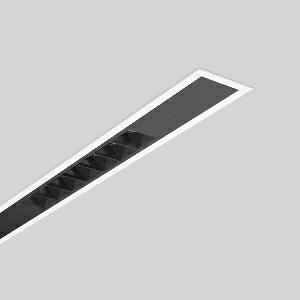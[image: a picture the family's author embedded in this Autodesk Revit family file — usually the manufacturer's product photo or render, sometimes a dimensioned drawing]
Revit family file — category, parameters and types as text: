
# Revit family: less_is_more_beamline_312465_002_76_12bc
name_source: partatom
category: Lighting Fixtures
units: mm (PartAtom-declared; Revit-internal decimal feet)

## family parameters
Cut with Voids When Loaded = No
Host = Face
Light Source = No
Part Type = Normal
Room Calculation Point = No
Round Connector Dimension = Use Diameter
Shared = No

## types (1)
- LESS IS MORE BEAMLINE (1 x LED Modul 930, 1025 lm, 3000)
    Apparent Load = 23 VA
    CIE Flux Codes = 100 100 100 100 100
    Color Rendering = 90
    Color Temperature = 3000
    Default Elevation = 1800 mm
    Description = Series: LESS IS MORE BEAMLINE
Linear recessed ceiling and wall luminaire for aesthetically sophisticated lighting. Luminaire with two LED light units. Housing: extruded aluminium profile, powder-coated. End cap aluminium powder-coated. LED light unit with MRS technology: Mini-Reflector-System made of metallised thermoplastic with prismatic black glare-suppressing frame for pleasant glare-free light (RUG < 10). Each LED light unit has 7 reflector elements. Narrow beam light distribution. Ceiling installation with pre-assembled SBS mounting system. LED unit with integrated converter interchangeable and removable. Suitable for through-wiring. 
Colour: traffic white, matt (RAL 9016)
Length: 1141 mm
Width: 71 mm
Height: 1.5 mm
Cut-out length: 1128 mm
Cut-out width: 60 mm
Recess height: 125 mm
Luminaire: recess height: 106 mm
Lamp: LED
Socket: without socket
Colour temperature: 3000K
Colour rendering index (CRI): 90
System power: 23 W
Rated luminous flux: 2050 lm
Luminous efficiency: 89 lm/W
Control gear: Converter, dimmable, DALI
Protection class: I
Type of protection: IP 20
    Height = 0 mm  [stored 0 ft]
    Lamp = 1 x LED Modul 930
    Lamp Light Flux = 1025 lm
    Lamp count = 1
    Length = 1141 mm
    Lifetime = 50000 h
    Luminous efficacy = 89 lm/W
    Manufacturer = RZB
    ModVariant = No
    Model = 312465.002.76
    Mounting Place = Ceiling, Wall
    Mounting Type = Recessed
    Number of Poles = 1
    OnlyDefault = Yes
    Power Factor = 1
    Product Name = LESS IS MORE BEAMLINE
    Product group = Recessed LED linear luminaires
    ProductGroupID = 407
    Protection Class = Protection class I
    Protection Degree = IP 20
    RLX_Detail_Level = 1
    RLX_Emergency_Light_Flux = 0 lm
    RLX_Emergency_Type = 0
    RLX_Emergency_Type_DB = No
    RlxData = <blob elided: 23713 chars, md5=9573ce2d>
    Socket = socket
    Standby Power = 0 W
    System Light Flux = 2050 lm
    System Power = 23 W
    Type Comments = Product without accessories
    Type Image = 312465.002.jpg
    URL = http://relux.com
    VarID = ---
    Voltage = 230 V
    Voltage Range = 220-240 V
    Weight = 0.00 kg
    Width = 71 mm

note: [stored X ft] marks values corroborated as IEEE doubles in the binary element streams (Revit-internal decimal feet)

## geometry (parser evidence)
native form markers: Blend x4, Sweep x16
no freeform markers — native parametric forms only
